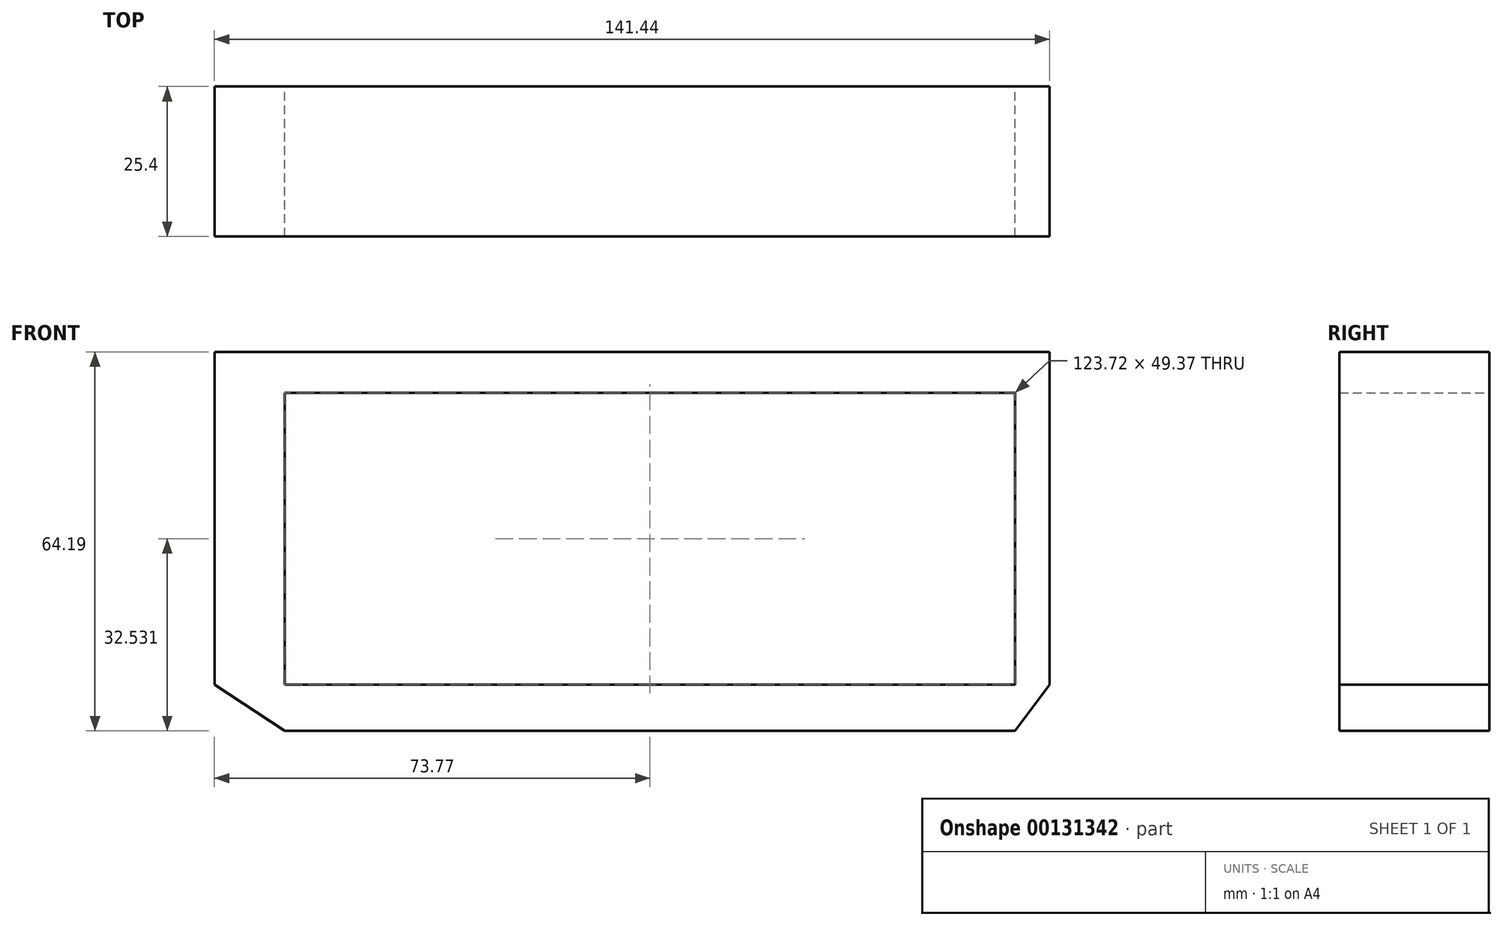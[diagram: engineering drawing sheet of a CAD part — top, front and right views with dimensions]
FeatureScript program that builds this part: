
annotation { "Feature Type Name" : "Feature", "Feature Type Description" : "" }
export const myFeature = defineFeature(function(context is Context, id is Id, definition is map)
    precondition{}
    {
        {
            var Q0;
            Q0=qCreatedBy(makeId("Front.planeOp"),FACE);
            var sketch = newSketch(context, id + "F0", { "sketchPlane" : qUnion([Q0])});
            skLineSegment(sketch, "E0.bottom", {"start": v(61.86, 28.6) * mm, "end": v(-61.86, 28.6) * mm});
            skLineSegment(sketch, "E0.top", {"start": v(61.86, -28.6) * mm, "end": v(-61.86, -28.6) * mm});
            skLineSegment(sketch, "E0.left", {"start": v(61.86, 28.6) * mm, "end": v(61.86, -28.6) * mm});
            skLineSegment(sketch, "E0.right", {"start": v(-61.86, 28.6) * mm, "end": v(-61.86, -28.6) * mm});
            skPoint(sketch, "E0.middle", {"position": v(0, 0) * mm});
            skLineSegment(sketch, "E1.bottom", {"start": v(-73.77, -20.76) * mm, "end": v(67.67, -20.76) * mm});
            skLineSegment(sketch, "E1.top", {"start": v(-73.77, 35.58) * mm, "end": v(67.67, 35.58) * mm});
            skLineSegment(sketch, "E1.left", {"start": v(-73.77, -20.76) * mm, "end": v(-73.77, 35.58) * mm});
            skLineSegment(sketch, "E1.right", {"start": v(67.67, -20.76) * mm, "end": v(67.67, 35.58) * mm});
            skLineSegment(sketch, "E2", {"start": v(-61.86, -28.6) * mm, "end": v(-73.77, -20.76) * mm});
            skLineSegment(sketch, "E3", {"start": v(-61.86, 28.6) * mm, "end": v(-73.77, 35.58) * mm});
            skLineSegment(sketch, "E4", {"start": v(61.86, -28.6) * mm, "end": v(67.67, -20.76) * mm});
            skLineSegment(sketch, "E5", {"start": v(61.86, 28.6) * mm, "end": v(67.67, 35.58) * mm});
            skLineSegment(sketch, "E6.bottom", {"start": v(-61.86, 28.6) * mm, "end": v(61.86, 28.6) * mm});
            skLineSegment(sketch, "E6.top", {"start": v(-61.86, -28.6) * mm, "end": v(61.86, -28.6) * mm});
            skSolve(sketch);
        }
        {
            var Q0;
            Q0 = qSketchRegion(id + "F0", true);
            var Q1;
            {var subQ5=sQuery(id+"F0.wireOp",EDGE,"E6.bottom");Q1=makeQuery(id+"F0.imprint","IMPRINT",FACE,{"disambiguationData":[TD([[makeQuery(id+"F0.imprint","IMPRINT",EDGE,{"derivedFrom":subQ5}),-1.0]])]});}
            extrude(context, id + "F1", {"entities" : qUnion([Q0, Q1]), "depth" : 25.4 * mm});
        }
    });
